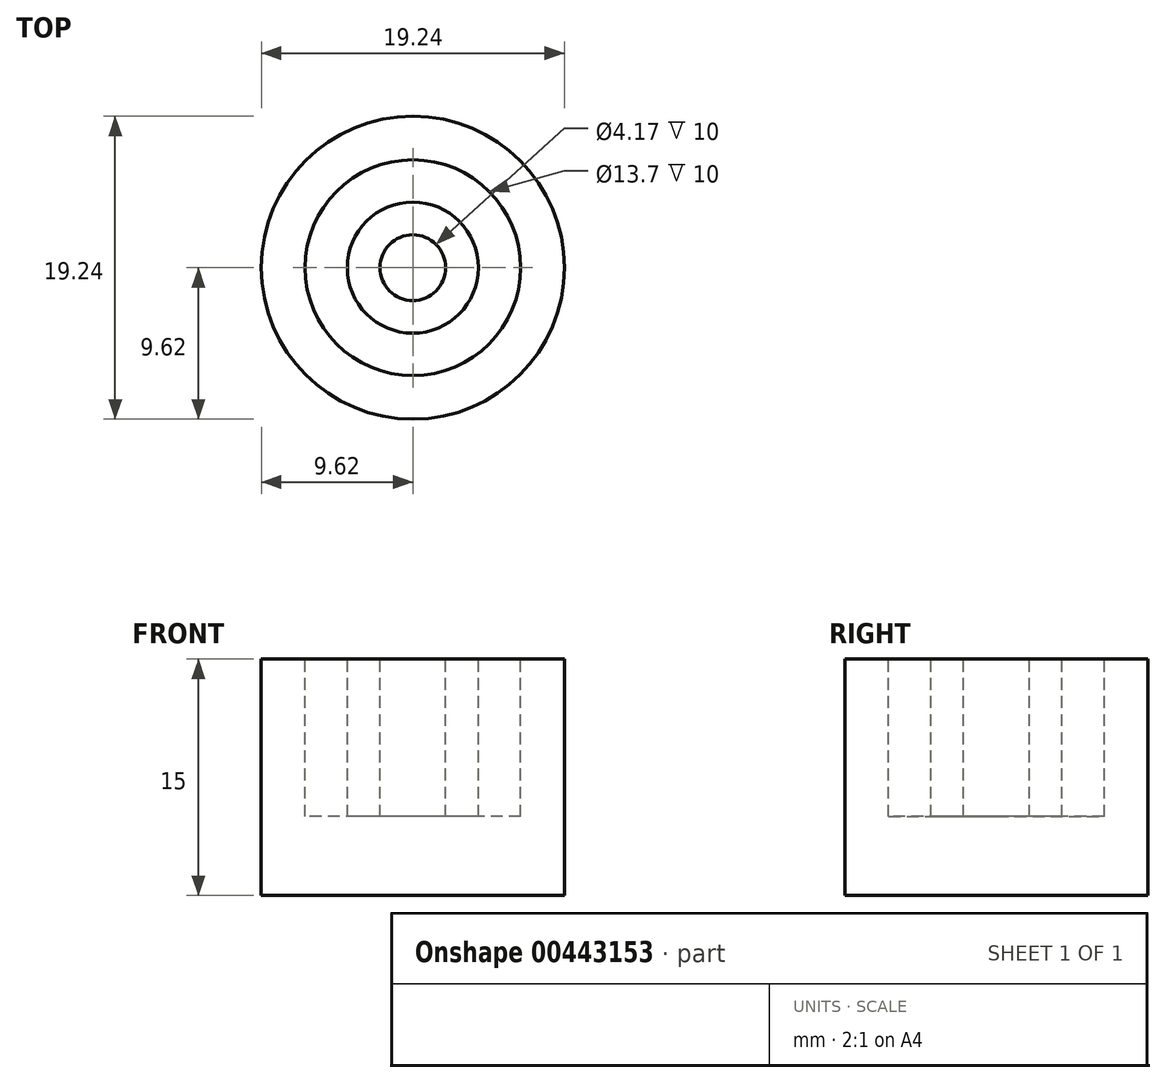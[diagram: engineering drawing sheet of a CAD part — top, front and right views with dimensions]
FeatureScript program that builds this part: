
annotation { "Feature Type Name" : "Feature", "Feature Type Description" : "" }
export const myFeature = defineFeature(function(context is Context, id is Id, definition is map)
    precondition{}
    {
        {
            var Q0;
            Q0=qCreatedBy(makeId("Top.planeOp"),FACE);
            var sketch = newSketch(context, id + "F0", { "sketchPlane" : qUnion([Q0])});
            skCircle(sketch, "E0", {"center": v(0, 0) * mm, "radius": 9.62 * mm});
            skSolve(sketch);
        }
        {
            var Q0;
            Q0=makeQuery(id+"F0.imprint","IMPRINT",FACE,{"disambiguationData":[TD([[makeQuery(id+"F0.imprint","IMPRINT",EDGE,{"derivedFrom":sQuery(id+"F0.wireOp",EDGE,"E0")}),1.0]])]});
            var Q1;
            Q1 = qSketchRegion(id + "F2", true);
            extrude(context, id + "F1", {"entities" : qUnion([Q0, Q1]), "depth" : 15 * mm});
        }
        {
            var Q0;
            Q0=makeQuery(id+"F1.opExtrude","CAP_FACE",FACE,{"disambiguationData":[OSD([sQuery(id+"F0.wireOp",EDGE,"E0")])],"isStart":false});
            var sketch = newSketch(context, id + "F2", { "sketchPlane" : qUnion([Q0])});
            skCircle(sketch, "E1", {"center": v(0, 0) * mm, "radius": 2.09 * mm});
            skCircle(sketch, "E2", {"center": v(0, 0) * mm, "radius": 4.16 * mm});
            skCircle(sketch, "E3", {"center": v(0, 0) * mm, "radius": 6.85 * mm});
            skSolve(sketch);
        }
        {
            var Q0;
            Q0=makeQuery(id+"F2.imprint","IMPRINT",FACE,{"disambiguationData":[TD([[makeQuery(id+"F2.imprint","IMPRINT",EDGE,{"derivedFrom":sQuery(id+"F2.wireOp",EDGE,"E1")}),1.0]])]});
            extrude(context, id + "F3", {"entities" : qUnion([Q0]), "operationType" : NewBodyOperationType.REMOVE, "oppositeDirection" : true, "depth" : 10 * mm});
        }
        {
            var Q0;
            Q0=makeQuery(id+"F2.imprint","IMPRINT",FACE,{"disambiguationData":[TD([[makeQuery(id+"F2.imprint","IMPRINT",EDGE,{"derivedFrom":sQuery(id+"F2.wireOp",EDGE,"E2")}),-1.0]])]});
            extrude(context, id + "F4", {"entities" : qUnion([Q0]), "operationType" : NewBodyOperationType.REMOVE, "oppositeDirection" : true, "depth" : 10 * mm});
        }
    });
